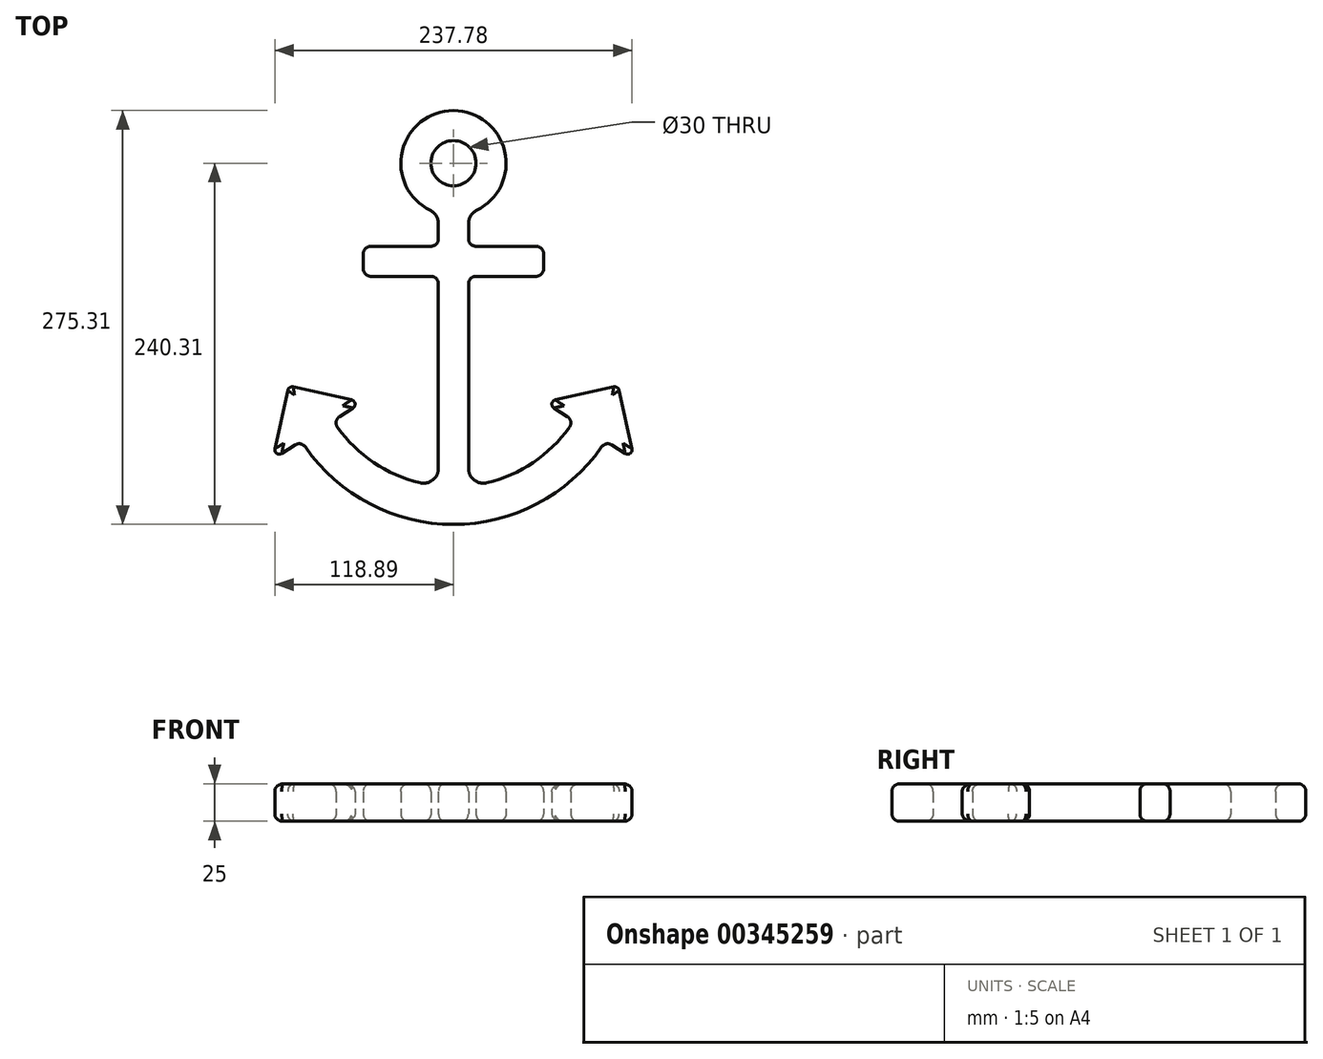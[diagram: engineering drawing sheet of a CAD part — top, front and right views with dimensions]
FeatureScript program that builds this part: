
annotation { "Feature Type Name" : "Feature", "Feature Type Description" : "" }
export const myFeature = defineFeature(function(context is Context, id is Id, definition is map)
    precondition{}
    {
        {
            var Q0;
            Q0=qCreatedBy(makeId("Top.planeOp"),FACE);
            var sketch = newSketch(context, id + "F0", { "sketchPlane" : qUnion([Q0])});
            skCircle(sketch, "E0", {"center": v(0, 0) * mm, "radius": 15 * mm});
            skArc(sketch, "E1", {"start": v(15.56, -31.35) * mm, "mid": v(0, 35) * mm, "end": v(-15.56, -31.35) * mm});
            skLineSegment(sketch, "E2.left", {"start": v(-10, -40.31) * mm, "end": v(-10, -50.31) * mm});
            skLineSegment(sketch, "E2.right", {"start": v(10, -40.31) * mm, "end": v(10, -50.31) * mm});
            skLineSegment(sketch, "E3.bottom", {"start": v(-55, -55.31) * mm, "end": v(-15, -55.31) * mm});
            skLineSegment(sketch, "E3.top", {"start": v(-55, -75.31) * mm, "end": v(-15, -75.31) * mm});
            skLineSegment(sketch, "E3.left", {"start": v(-60, -60.31) * mm, "end": v(-60, -70.31) * mm});
            skPoint(sketch, "E4.visualSharp", {"position": v(10, -33.54) * mm});
            skArc(sketch, "E4.filletArc", {"start": v(15.56, -31.35) * mm, "mid": v(11.5, -35.04) * mm, "end": v(10, -40.31) * mm});
            skPoint(sketch, "E5.visualSharp", {"position": v(-10, -33.54) * mm});
            skArc(sketch, "E5.filletArc", {"start": v(-10, -40.31) * mm, "mid": v(-11.5, -35.04) * mm, "end": v(-15.56, -31.35) * mm});
            skLineSegment(sketch, "E6.MirrorCS", {"start": v(55, -55.31) * mm, "end": v(15, -55.31) * mm});
            skLineSegment(sketch, "E7.MirrorCS", {"start": v(55, -75.31) * mm, "end": v(15, -75.31) * mm});
            skLineSegment(sketch, "E8.MirrorCS", {"start": v(60, -60.31) * mm, "end": v(60, -70.31) * mm});
            skArc(sketch, "E9", {"start": v(-77.16, -175.73) * mm, "mid": v(-53.07, -199.1) * mm, "end": v(-22.35, -212.64) * mm});
            skLineSegment(sketch, "E10.trimOffspring", {"start": v(-10, -80.31) * mm, "end": v(-10, -202.92) * mm});
            skLineSegment(sketch, "E11.trimOffspring", {"start": v(10, -80.31) * mm, "end": v(10, -202.92) * mm});
            skArc(sketch, "E12", {"start": v(-98.55, -188.78) * mm, "mid": v(0, -240.31) * mm, "end": v(98.55, -188.78) * mm});
            skPoint(sketch, "E13.visualSharp", {"position": v(-60, -55.31) * mm});
            skArc(sketch, "E13.filletArc", {"start": v(-55, -55.31) * mm, "mid": v(-58.54, -56.78) * mm, "end": v(-60, -60.31) * mm});
            skPoint(sketch, "E14.visualSharp", {"position": v(-60, -75.31) * mm});
            skArc(sketch, "E14.filletArc", {"start": v(-60, -70.31) * mm, "mid": v(-58.54, -73.85) * mm, "end": v(-55, -75.31) * mm});
            skPoint(sketch, "E15.visualSharp", {"position": v(60, -75.31) * mm});
            skArc(sketch, "E15.filletArc", {"start": v(55, -75.31) * mm, "mid": v(58.54, -73.85) * mm, "end": v(60, -70.31) * mm});
            skPoint(sketch, "E16.visualSharp", {"position": v(60, -55.31) * mm});
            skArc(sketch, "E16.filletArc", {"start": v(60, -60.31) * mm, "mid": v(58.54, -56.78) * mm, "end": v(55, -55.31) * mm});
            skLineSegment(sketch, "E17", {"start": v(-118.81, -189.93) * mm, "end": v(-110.2, -151.12) * mm});
            skLineSegment(sketch, "E18", {"start": v(-106.63, -148.84) * mm, "end": v(-67.82, -157.44) * mm});
            skLineSegment(sketch, "E19", {"start": v(-57.1, -254.02) * mm, "end": v(-101.2, -184.79) * mm, "construction": true});
            skPoint(sketch, "E20.visualSharp", {"position": v(-60.75, -159.01) * mm});
            skArc(sketch, "E20.filletArc", {"start": v(-66.85, -162.9) * mm, "mid": v(-65.51, -159.85) * mm, "end": v(-67.82, -157.44) * mm});
            skPoint(sketch, "E21.visualSharp", {"position": v(-109.56, -148.19) * mm});
            skArc(sketch, "E21.filletArc", {"start": v(-106.63, -148.84) * mm, "mid": v(-108.9, -149.24) * mm, "end": v(-110.2, -151.12) * mm});
            skPoint(sketch, "E22.visualSharp", {"position": v(-120.38, -197) * mm});
            skArc(sketch, "E22.filletArc", {"start": v(-118.81, -189.93) * mm, "mid": v(-117.6, -193.04) * mm, "end": v(-114.27, -193.11) * mm});
            skArc(sketch, "E23.trimOffspring", {"start": v(22.35, -212.64) * mm, "mid": v(53.07, -199.1) * mm, "end": v(77.16, -175.73) * mm});
            skPoint(sketch, "E24.visualSharp", {"position": v(10, -214.78) * mm});
            skArc(sketch, "E24.filletArc", {"start": v(10, -202.92) * mm, "mid": v(13.82, -210.78) * mm, "end": v(22.35, -212.64) * mm});
            skPoint(sketch, "E25.visualSharp", {"position": v(-10, -214.78) * mm});
            skArc(sketch, "E25.filletArc", {"start": v(-22.35, -212.64) * mm, "mid": v(-13.82, -210.78) * mm, "end": v(-10, -202.92) * mm});
            skLineSegment(sketch, "E26", {"start": v(-66.85, -162.9) * mm, "end": v(-75.79, -168.6) * mm});
            skLineSegment(sketch, "E27", {"start": v(-105.34, -187.42) * mm, "end": v(-114.27, -193.11) * mm});
            skLineSegment(sketch, "E28", {"start": v(-101.2, -184.79) * mm, "end": v(-80.12, -171.35) * mm, "construction": true});
            skArc(sketch, "E29.MirrorCS", {"start": v(106.63, -148.84) * mm, "mid": v(108.9, -149.24) * mm, "end": v(110.2, -151.12) * mm});
            skArc(sketch, "E30.MirrorCS", {"start": v(66.85, -162.9) * mm, "mid": v(65.51, -159.85) * mm, "end": v(67.82, -157.44) * mm});
            skLineSegment(sketch, "E31.MirrorCS", {"start": v(105.34, -187.42) * mm, "end": v(114.27, -193.11) * mm});
            skArc(sketch, "E32.MirrorCS", {"start": v(118.81, -189.93) * mm, "mid": v(117.6, -193.04) * mm, "end": v(114.27, -193.11) * mm});
            skLineSegment(sketch, "E33.MirrorCS", {"start": v(66.85, -162.9) * mm, "end": v(75.79, -168.6) * mm});
            skPoint(sketch, "E34.MirrorP", {"position": v(60.75, -159.01) * mm});
            skLineSegment(sketch, "E35.MirrorCS", {"start": v(118.81, -189.93) * mm, "end": v(110.2, -151.12) * mm});
            skPoint(sketch, "E36.MirrorP", {"position": v(109.56, -148.19) * mm});
            skLineSegment(sketch, "E37.MirrorCS", {"start": v(106.63, -148.84) * mm, "end": v(67.82, -157.44) * mm});
            skLineSegment(sketch, "E38.MirrorCS", {"start": v(101.2, -184.79) * mm, "end": v(80.12, -171.35) * mm, "construction": true});
            skPoint(sketch, "E39.MirrorP", {"position": v(120.38, -197) * mm});
            skPoint(sketch, "E40.visualSharp", {"position": v(-80.12, -171.35) * mm});
            skArc(sketch, "E40.filletArc", {"start": v(-75.79, -168.6) * mm, "mid": v(-78.01, -171.86) * mm, "end": v(-77.16, -175.73) * mm});
            skPoint(sketch, "E41.visualSharp", {"position": v(-101.2, -184.79) * mm});
            skArc(sketch, "E41.filletArc", {"start": v(-98.55, -188.78) * mm, "mid": v(-101.67, -186.73) * mm, "end": v(-105.34, -187.42) * mm});
            skPoint(sketch, "E42.visualSharp", {"position": v(101.2, -184.79) * mm});
            skArc(sketch, "E42.filletArc", {"start": v(105.34, -187.42) * mm, "mid": v(101.67, -186.73) * mm, "end": v(98.55, -188.78) * mm});
            skPoint(sketch, "E43.visualSharp", {"position": v(80.12, -171.35) * mm});
            skArc(sketch, "E43.filletArc", {"start": v(77.16, -175.73) * mm, "mid": v(78.01, -171.86) * mm, "end": v(75.79, -168.6) * mm});
            skPoint(sketch, "E44.visualSharp", {"position": v(-10, -55.31) * mm});
            skArc(sketch, "E44.filletArc", {"start": v(-15, -55.31) * mm, "mid": v(-11.46, -53.85) * mm, "end": v(-10, -50.31) * mm});
            skPoint(sketch, "E45.visualSharp", {"position": v(-10, -75.31) * mm});
            skArc(sketch, "E45.filletArc", {"start": v(-10, -80.31) * mm, "mid": v(-11.46, -76.78) * mm, "end": v(-15, -75.31) * mm});
            skPoint(sketch, "E46.visualSharp", {"position": v(10, -75.31) * mm});
            skArc(sketch, "E46.filletArc", {"start": v(15, -75.31) * mm, "mid": v(11.46, -76.78) * mm, "end": v(10, -80.31) * mm});
            skPoint(sketch, "E47.visualSharp", {"position": v(10, -55.31) * mm});
            skArc(sketch, "E47.filletArc", {"start": v(10, -50.31) * mm, "mid": v(11.46, -53.85) * mm, "end": v(15, -55.31) * mm});
            skSolve(sketch);
        }
        {
            var Q0;
            Q0=makeQuery(id+"F0.imprint","IMPRINT",FACE,{"disambiguationData":[TD([[makeQuery(id+"F0.imprint","IMPRINT",EDGE,{"derivedFrom":sQuery(id+"F0.wireOp",EDGE,"E0")}),-1.0]])]});
            var Q1;
            {var subQ6=sQuery(id+"F0.wireOp",EDGE,"E12");Q1=makeQuery(id+"F0.imprint","IMPRINT",FACE,{"disambiguationData":[TD([[makeQuery(id+"F0.imprint","IMPRINT",EDGE,{"derivedFrom":subQ6}),1.0]])]});}
            var Q2;
            Q2=makeQuery(id+"F0.imprint","IMPRINT",FACE,{"disambiguationData":[TD([[makeQuery(id+"F0.imprint","IMPRINT",EDGE,{"derivedFrom":sQuery(id+"F0.wireOp",EDGE,"E17")}),-1.0]])]});
            var Q3;
            Q3=makeQuery(id+"F0.imprint","IMPRINT",FACE,{"disambiguationData":[TD([[makeQuery(id+"F0.imprint","IMPRINT",EDGE,{"derivedFrom":sQuery(id+"F0.wireOp",EDGE,"288954a1-4b5b-4858-b1c7-edba4a30fe570.MirrorCS")}),-1.0]])]});
            extrude(context, id + "F1", {"entities" : qUnion([Q0, Q1, Q2, Q3]), "depth" : 25 * mm});
        }
        {
            var Q0;
            Q0=makeQuery(id+"F1.opExtrude","CAP_EDGE",EDGE,{"disambiguationData":[OSD([sQuery(id+"F0.wireOp",EDGE,"E10.trimOffspring")])],"isStart":false});
            var Q1;
            Q1=makeQuery(id+"F1.opExtrude","CAP_EDGE",EDGE,{"disambiguationData":[OSD([sQuery(id+"F0.wireOp",EDGE,"E3.top")])],"isStart":false});
            var Q2;
            Q2=makeQuery(id+"F1.opExtrude","CAP_EDGE",EDGE,{"disambiguationData":[OSD([sQuery(id+"F0.wireOp",EDGE,"E2.left")])],"isStart":false});
            var Q3;
            Q3=makeQuery(id+"F1.opExtrude","CAP_EDGE",EDGE,{"disambiguationData":[OSD([sQuery(id+"F0.wireOp",EDGE,"E6.MirrorCS")])],"isStart":false});
            var Q4;
            Q4=makeQuery(id+"F1.opExtrude","CAP_EDGE",EDGE,{"disambiguationData":[OSD([sQuery(id+"F0.wireOp",EDGE,"E11.trimOffspring")])],"isStart":false});
            var Q5;
            {var subQ0=sQuery(id+"F0.wireOp",EDGE,"E9");Q5=makeQuery(id+"F1.opExtrude","CAP_EDGE",EDGE,{"disambiguationData":[OSD([subQ0]),TDD([makeQuery(id+"F0.imprint","IMPRINT",EDGE,{"disambiguationData":[TD([[makeQuery(id+"F0.imprint","INTERSECT",VERTEX,{"derivedFrom":[subQ0,sQuery(id+"F0.wireOp",EDGE,"288954a1-4b5b-4858-b1c7-edba4a30fe575.MirrorCS")]}),1.0]])],"derivedFrom":subQ0})])],"isStart":false});}
            var Q6;
            Q6=makeQuery(id+"F1.opExtrude","CAP_EDGE",EDGE,{"disambiguationData":[OSD([sQuery(id+"F0.wireOp",EDGE,"288954a1-4b5b-4858-b1c7-edba4a30fe5711.MirrorCS")])],"isStart":false});
            var Q7;
            Q7=makeQuery(id+"F1.opExtrude","CAP_EDGE",EDGE,{"disambiguationData":[OSD([sQuery(id+"F0.wireOp",EDGE,"E12")])],"isStart":false});
            var Q8;
            {var subQ0=sQuery(id+"F0.wireOp",EDGE,"E9");Q8=makeQuery(id+"F1.opExtrude","CAP_EDGE",EDGE,{"disambiguationData":[OSD([subQ0]),TDD([makeQuery(id+"F0.imprint","IMPRINT",EDGE,{"disambiguationData":[TD([[makeQuery(id+"F0.imprint","INTERSECT",VERTEX,{"derivedFrom":[subQ0,sQuery(id+"F0.wireOp",EDGE,"nB2go7IL-jNhh-HqPr-qVcc-Enntn88Nk1QF")]}),-1.0]])],"derivedFrom":subQ0})])],"isStart":false});}
            var Q9;
            {var subQ0=sQuery(id+"F0.wireOp",EDGE,"nB2go7IL-jNhh-HqPr-qVcc-Enntn88Nk1QF");Q9=makeQuery(id+"F1.opExtrude","CAP_EDGE",EDGE,{"disambiguationData":[OSD([subQ0]),TDD([makeQuery(id+"F0.imprint","IMPRINT",EDGE,{"disambiguationData":[TD([[makeQuery(id+"F0.imprint","INTERSECT",VERTEX,{"derivedFrom":[sQuery(id+"F0.wireOp",EDGE,"E9"),subQ0]}),1.0]])],"derivedFrom":subQ0})])],"isStart":false});}
            var Q10;
            Q10=makeQuery(id+"F1.opExtrude","CAP_EDGE",EDGE,{"disambiguationData":[OSD([sQuery(id+"F0.wireOp",EDGE,"E12")])],"isStart":true});
            var Q11;
            {var subQ0=sQuery(id+"F0.wireOp",EDGE,"E9");Q11=makeQuery(id+"F1.opExtrude","CAP_EDGE",EDGE,{"disambiguationData":[OSD([subQ0]),TDD([makeQuery(id+"F0.imprint","IMPRINT",EDGE,{"disambiguationData":[TD([[makeQuery(id+"F0.imprint","INTERSECT",VERTEX,{"derivedFrom":[subQ0,sQuery(id+"F0.wireOp",EDGE,"288954a1-4b5b-4858-b1c7-edba4a30fe575.MirrorCS")]}),1.0]])],"derivedFrom":subQ0})])],"isStart":true});}
            var Q12;
            Q12=makeQuery(id+"F1.opExtrude","CAP_EDGE",EDGE,{"disambiguationData":[OSD([sQuery(id+"F0.wireOp",EDGE,"288954a1-4b5b-4858-b1c7-edba4a30fe5711.MirrorCS")])],"isStart":true});
            var Q13;
            Q13=makeQuery(id+"F1.opExtrude","CAP_EDGE",EDGE,{"disambiguationData":[OSD([sQuery(id+"F0.wireOp",EDGE,"E11.trimOffspring")])],"isStart":true});
            var Q14;
            Q14=makeQuery(id+"F1.opExtrude","CAP_EDGE",EDGE,{"disambiguationData":[OSD([sQuery(id+"F0.wireOp",EDGE,"E3.bottom")])],"isStart":true});
            var Q15;
            Q15=makeQuery(id+"F1.opExtrude","CAP_EDGE",EDGE,{"disambiguationData":[OSD([sQuery(id+"F0.wireOp",EDGE,"E2.right")])],"isStart":true});
            var Q16;
            Q16=makeQuery(id+"F1.opExtrude","CAP_EDGE",EDGE,{"disambiguationData":[OSD([sQuery(id+"F0.wireOp",EDGE,"E6.MirrorCS")])],"isStart":true});
            var Q17;
            {var subQ0=sQuery(id+"F0.wireOp",EDGE,"E9");Q17=makeQuery(id+"F1.opExtrude","CAP_EDGE",EDGE,{"disambiguationData":[OSD([subQ0]),TDD([makeQuery(id+"F0.imprint","IMPRINT",EDGE,{"disambiguationData":[TD([[makeQuery(id+"F0.imprint","INTERSECT",VERTEX,{"derivedFrom":[subQ0,sQuery(id+"F0.wireOp",EDGE,"nB2go7IL-jNhh-HqPr-qVcc-Enntn88Nk1QF")]}),-1.0]])],"derivedFrom":subQ0})])],"isStart":true});}
            var Q18;
            Q18=makeQuery(id+"F1.opExtrude","CAP_EDGE",EDGE,{"disambiguationData":[OSD([sQuery(id+"F0.wireOp",EDGE,"E18")])],"isStart":true});
            var Q19;
            Q19=makeQuery(id+"F1.opExtrude","CAP_EDGE",EDGE,{"disambiguationData":[OSD([sQuery(id+"F0.wireOp",EDGE,"E10.trimOffspring")])],"isStart":true});
            var Q20;
            Q20=makeQuery(id+"F1.opExtrude","CAP_EDGE",EDGE,{"disambiguationData":[OSD([sQuery(id+"F0.wireOp",EDGE,"E0")])],"isStart":true});
            var Q21;
            Q21=makeQuery(id+"F1.opExtrude","CAP_EDGE",EDGE,{"disambiguationData":[OSD([sQuery(id+"F0.wireOp",EDGE,"E0")])],"isStart":false});
            fillet(context, id + "F2", {"entities" : qUnion([Q0, Q1, Q2, Q3, Q4, Q5, Q6, Q7, Q8, Q9, Q10, Q11, Q12, Q13, Q14, Q15, Q16, Q17, Q18, Q19, Q20, Q21]), "radius" : 5 * mm, "tangentPropagation" : true, "allowEdgeOverflow" : false});
        }
    });
